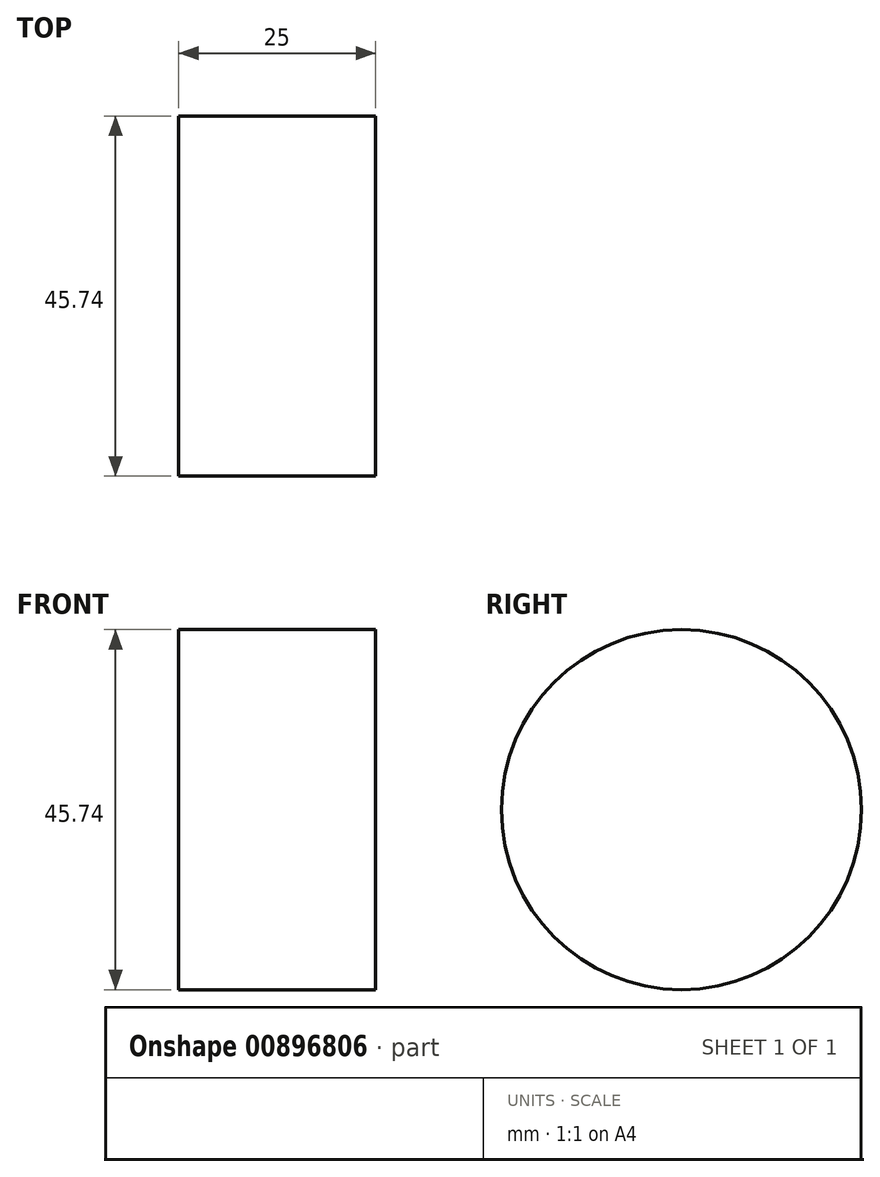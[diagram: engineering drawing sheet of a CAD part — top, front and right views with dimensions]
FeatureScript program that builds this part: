
annotation { "Feature Type Name" : "Feature", "Feature Type Description" : "" }
export const myFeature = defineFeature(function(context is Context, id is Id, definition is map)
    precondition{}
    {
        {
            var Q0;
            Q0=qCreatedBy(makeId("Right.planeOp"),FACE);
            var sketch = newSketch(context, id + "F0", { "sketchPlane" : qUnion([Q0])});
            skCircle(sketch, "E0", {"center": v(-41.3, 17.06) * mm, "radius": 22.87 * mm});
            skCircle(sketch, "E1", {"center": v(-41.3, 17.06) * mm, "radius": 16.92 * mm});
            skSolve(sketch);
        }
        {
            var Q0;
            Q0=sQuery(id+"F0.wireOp",EDGE,"E0");
            extrude(context, id + "F1", {"bodyType" : ToolBodyType.SURFACE, "surfaceEntities" : qUnion([Q0]), "endBound" : BoundingType.SYMMETRIC, "depth" : 25 * mm, "offsetDistance" : 25 * mm});
        }
    });
